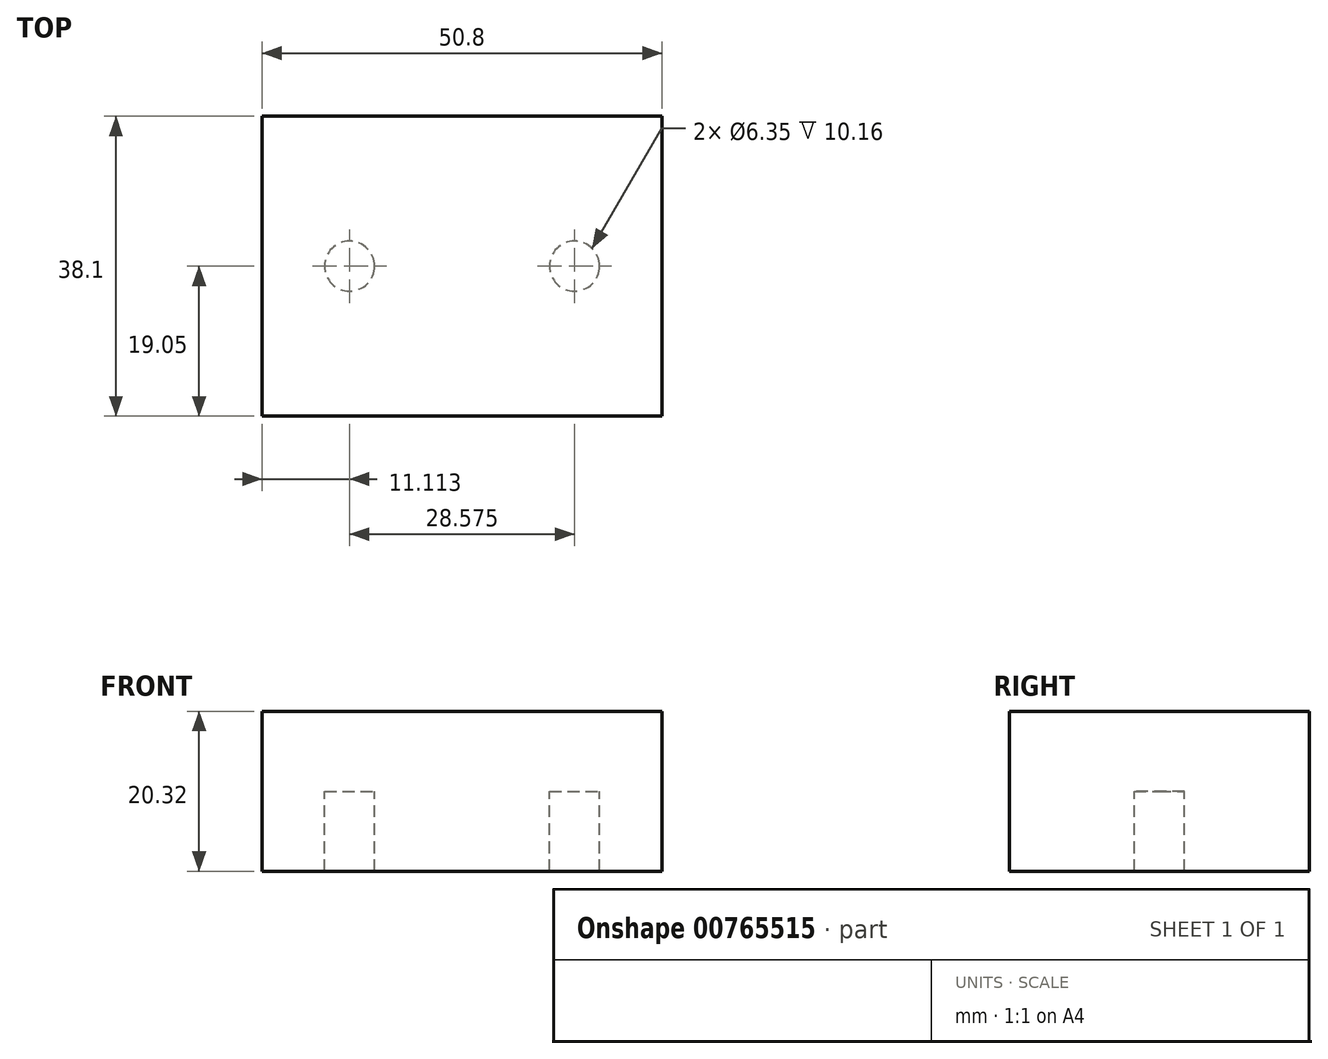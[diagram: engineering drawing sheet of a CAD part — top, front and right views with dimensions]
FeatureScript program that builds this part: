
annotation { "Feature Type Name" : "Feature", "Feature Type Description" : "" }
export const myFeature = defineFeature(function(context is Context, id is Id, definition is map)
    precondition{}
    {
        {
            var Q0;
            Q0=qCreatedBy(makeId("Top.planeOp"),FACE);
            var sketch = newSketch(context, id + "F0", { "sketchPlane" : qUnion([Q0])});
            skLineSegment(sketch, "E0.bottom", {"start": v(0, 0) * mm, "end": v(50.8, 0) * mm});
            skLineSegment(sketch, "E0.top", {"start": v(0, 25.4) * mm, "end": v(50.8, 25.4) * mm});
            skLineSegment(sketch, "E0.left", {"start": v(0, 0) * mm, "end": v(0, 25.4) * mm});
            skLineSegment(sketch, "E0.right", {"start": v(50.8, 0) * mm, "end": v(50.8, 25.4) * mm});
            skSolve(sketch);
        }
        {
            var Q0;
            Q0=makeQuery(id+"F0.imprint","IMPRINT",FACE,{"disambiguationData":[TD([[makeQuery(id+"F0.imprint","IMPRINT",EDGE,{"derivedFrom":sQuery(id+"F0.wireOp",EDGE,"E0.bottom")}),1.0]])]});
            extrude(context, id + "F1", {"entities" : qUnion([Q0]), "depth" : 10.16 * mm, "offsetDistance" : 25.4 * mm});
        }
        {
            var Q0;
            Q0=makeQuery(id+"F1.opExtrude","CAP_FACE",FACE,{"disambiguationData":[OSD([sQuery(id+"F0.wireOp",EDGE,"E0.bottom"),sQuery(id+"F0.wireOp",EDGE,"E0.top"),sQuery(id+"F0.wireOp",EDGE,"E0.left"),sQuery(id+"F0.wireOp",EDGE,"E0.right")])],"isStart":true});
            var sketch = newSketch(context, id + "F2", { "sketchPlane" : qUnion([Q0])});
            skCircle(sketch, "E1", {"center": v(25.4, -12.7) * mm, "radius": 3.18 * mm});
            skPoint(sketch, "E1.centerSnap0", {"position": v(0, -12.7) * mm});
            skPoint(sketch, "E1.centerSnap1", {"position": v(25.4, 0) * mm});
            skSolve(sketch);
        }
        {
            var Q0;
            Q0=makeQuery(id+"F2.imprint","IMPRINT",FACE,{"disambiguationData":[TD([[makeQuery(id+"F2.imprint","IMPRINT",EDGE,{"derivedFrom":sQuery(id+"F2.wireOp",EDGE,"E1")}),1.0]])]});
            extrude(context, id + "F3", {"entities" : qUnion([Q0]), "operationType" : NewBodyOperationType.ADD, "depth" : 10.16 * mm, "offsetDistance" : 25.4 * mm});
        }
        {
            var Q0;
            Q0=makeQuery(id+"F1.opExtrude","CAP_FACE",FACE,{"disambiguationData":[OSD([sQuery(id+"F0.wireOp",EDGE,"E0.bottom"),sQuery(id+"F0.wireOp",EDGE,"E0.top"),sQuery(id+"F0.wireOp",EDGE,"E0.left"),sQuery(id+"F0.wireOp",EDGE,"E0.right")])],"isStart":true});
            var sketch = newSketch(context, id + "F4", { "sketchPlane" : qUnion([Q0])});
            skLineSegment(sketch, "E2", {"start": v(0, -12.7) * mm, "end": v(22.23, -12.7) * mm});
            skCircle(sketch, "E3", {"center": v(11.11, -12.7) * mm, "radius": 3.18 * mm});
            skLineSegment(sketch, "E4", {"start": v(50.8, -12.7) * mm, "end": v(28.58, -12.7) * mm});
            skCircle(sketch, "E5", {"center": v(39.69, -12.7) * mm, "radius": 3.18 * mm});
            skSolve(sketch);
        }
        {
            var Q0;
            {var subQ0=sQuery(id+"F4.wireOp",EDGE,"E3");var subQ1=sQuery(id+"F4.wireOp",EDGE,"E2");var subQ2=makeQuery(id+"F4.imprint","INTERSECT",VERTEX,{"disambiguationData":[OD(0.0)],"derivedFrom":[subQ1,subQ0]});Q0=makeQuery(id+"F4.imprint","IMPRINT",FACE,{"disambiguationData":[TD([[makeQuery(id+"F4.imprint","IMPRINT",EDGE,{"disambiguationData":[TD([[subQ2,-1.0]])],"derivedFrom":subQ1}),1.0]])]});}
            var Q1;
            {var subQ0=sQuery(id+"F4.wireOp",EDGE,"E3");var subQ1=sQuery(id+"F4.wireOp",EDGE,"E2");var subQ2=makeQuery(id+"F4.imprint","INTERSECT",VERTEX,{"disambiguationData":[OD(0.0)],"derivedFrom":[subQ1,subQ0]});Q1=makeQuery(id+"F4.imprint","IMPRINT",FACE,{"disambiguationData":[TD([[makeQuery(id+"F4.imprint","IMPRINT",EDGE,{"disambiguationData":[TD([[subQ2,-1.0]])],"derivedFrom":subQ1}),-1.0]])]});}
            var Q2;
            {var subQ0=sQuery(id+"F4.wireOp",EDGE,"E5");var subQ1=sQuery(id+"F4.wireOp",EDGE,"E4");var subQ2=makeQuery(id+"F4.imprint","INTERSECT",VERTEX,{"disambiguationData":[OD(0.0)],"derivedFrom":[subQ1,subQ0]});Q2=makeQuery(id+"F4.imprint","IMPRINT",FACE,{"disambiguationData":[TD([[makeQuery(id+"F4.imprint","IMPRINT",EDGE,{"disambiguationData":[TD([[subQ2,-1.0]])],"derivedFrom":subQ1}),1.0]])]});}
            var Q3;
            {var subQ0=sQuery(id+"F4.wireOp",EDGE,"E5");var subQ1=sQuery(id+"F4.wireOp",EDGE,"E4");var subQ2=makeQuery(id+"F4.imprint","INTERSECT",VERTEX,{"disambiguationData":[OD(0.0)],"derivedFrom":[subQ1,subQ0]});Q3=makeQuery(id+"F4.imprint","IMPRINT",FACE,{"disambiguationData":[TD([[makeQuery(id+"F4.imprint","IMPRINT",EDGE,{"disambiguationData":[TD([[subQ2,-1.0]])],"derivedFrom":subQ1}),-1.0]])]});}
            extrude(context, id + "F5", {"entities" : qUnion([Q0, Q1, Q2, Q3]), "operationType" : NewBodyOperationType.ADD, "depth" : 10.16 * mm, "offsetDistance" : 25.4 * mm});
        }
        {
            var Q0;
            Q0=makeQuery(id+"F1.opExtrude","SWEPT_FACE",FACE,{"disambiguationData":[OSD([sQuery(id+"F0.wireOp",EDGE,"E0.bottom")])]});
            extrude(context, id + "F6", {"entities" : qUnion([Q0]), "operationType" : NewBodyOperationType.ADD, "depth" : 6.35 * mm, "offsetDistance" : 25.4 * mm});
        }
        {
            var Q0;
            Q0=makeQuery(id+"F1.opExtrude","SWEPT_FACE",FACE,{"disambiguationData":[OSD([sQuery(id+"F0.wireOp",EDGE,"E0.top")])]});
            extrude(context, id + "F7", {"entities" : qUnion([Q0]), "operationType" : NewBodyOperationType.ADD, "depth" : 6.35 * mm, "offsetDistance" : 25.4 * mm});
        }
    });
